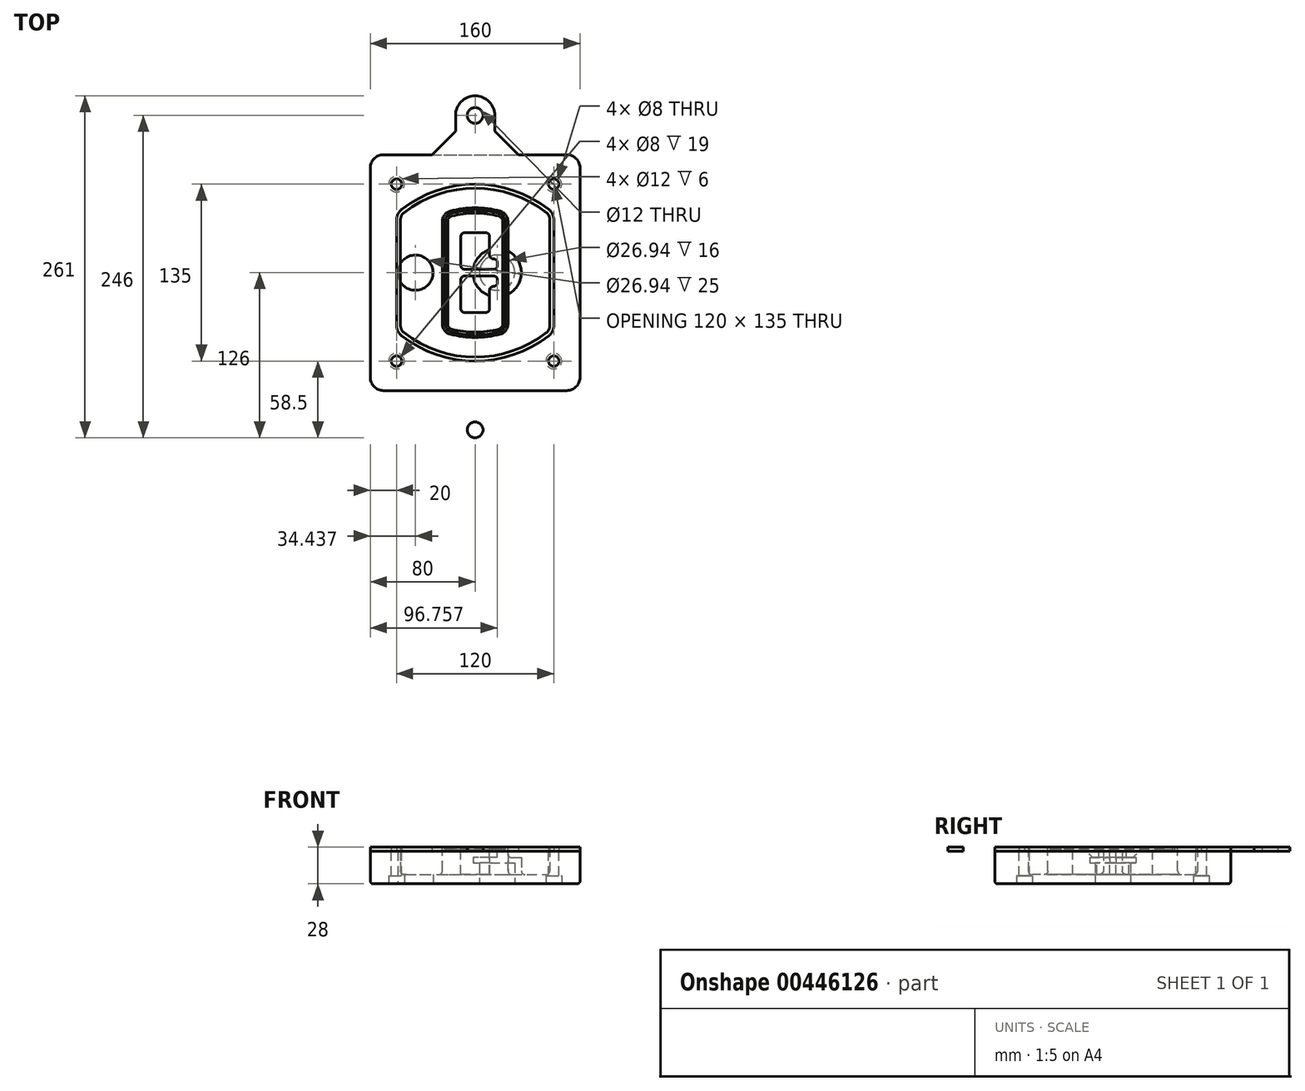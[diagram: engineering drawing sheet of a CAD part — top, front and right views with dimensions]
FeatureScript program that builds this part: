
annotation { "Feature Type Name" : "Feature", "Feature Type Description" : "" }
export const myFeature = defineFeature(function(context is Context, id is Id, definition is map)
    precondition{}
    {
        {
            var Q0;
            Q0=qCreatedBy(makeId("Top.planeOp"),FACE);
            var sketch = newSketch(context, id + "F0", { "sketchPlane" : qUnion([Q0])});
            skPoint(sketch, "E0.rect.middle", {"position": v(0, 0) * mm});
            skLineSegment(sketch, "E1.bottom", {"start": v(-70, -90) * mm, "end": v(70, -90) * mm});
            skLineSegment(sketch, "E1.top", {"start": v(-70, 90) * mm, "end": v(70, 90) * mm});
            skLineSegment(sketch, "E1.left", {"start": v(-80, -80) * mm, "end": v(-80, 80) * mm});
            skLineSegment(sketch, "E1.right", {"start": v(80, -80) * mm, "end": v(80, 80) * mm});
            skLineSegment(sketch, "E2", {"start": v(-80, 90) * mm, "end": v(80, -90) * mm, "construction": true});
            skLineSegment(sketch, "E3", {"start": v(80, 90) * mm, "end": v(-80, -90) * mm, "construction": true});
            skCircle(sketch, "E4", {"center": v(-60, 67.5) * mm, "radius": 4 * mm});
            skCircle(sketch, "E5", {"center": v(60, 67.5) * mm, "radius": 4 * mm});
            skCircle(sketch, "E6", {"center": v(60, -67.5) * mm, "radius": 4 * mm});
            skCircle(sketch, "E7", {"center": v(-60, -67.5) * mm, "radius": 4 * mm});
            skLineSegment(sketch, "E8", {"start": v(-60, 67.5) * mm, "end": v(60, 67.5) * mm, "construction": true});
            skLineSegment(sketch, "E9", {"start": v(60, 67.5) * mm, "end": v(60, -67.5) * mm, "construction": true});
            skLineSegment(sketch, "E10", {"start": v(60, -67.5) * mm, "end": v(-60, -67.5) * mm, "construction": true});
            skLineSegment(sketch, "E11", {"start": v(-60, -67.5) * mm, "end": v(-60, 67.5) * mm, "construction": true});
            skLineSegment(sketch, "E12", {"start": v(-60, 40.3) * mm, "end": v(-60, -40.3) * mm});
            skLineSegment(sketch, "E13", {"start": v(60, 40.3) * mm, "end": v(60, -40.3) * mm});
            skArc(sketch, "E14", {"start": v(56.15, 48.18) * mm, "mid": v(0, 67.5) * mm, "end": v(-56.15, 48.18) * mm});
            skArc(sketch, "E15", {"start": v(-56.15, -48.18) * mm, "mid": v(0, -67.5) * mm, "end": v(56.15, -48.18) * mm});
            skLineSegment(sketch, "E16", {"start": v(-60, 0) * mm, "end": v(60, 0) * mm, "construction": true});
            skPoint(sketch, "E17.visualSharp", {"position": v(-60, -45) * mm});
            skArc(sketch, "E17.filletArc", {"start": v(-60, -40.3) * mm, "mid": v(-58.99, -44.68) * mm, "end": v(-56.15, -48.18) * mm});
            skPoint(sketch, "E18.visualSharp", {"position": v(-60, 45) * mm});
            skArc(sketch, "E18.filletArc", {"start": v(-56.15, 48.18) * mm, "mid": v(-58.99, 44.68) * mm, "end": v(-60, 40.3) * mm});
            skPoint(sketch, "E19.visualSharp", {"position": v(60, 45) * mm});
            skArc(sketch, "E19.filletArc", {"start": v(60, 40.3) * mm, "mid": v(58.99, 44.68) * mm, "end": v(56.15, 48.18) * mm});
            skPoint(sketch, "E20.visualSharp", {"position": v(60, -45) * mm});
            skArc(sketch, "E20.filletArc", {"start": v(56.15, -48.18) * mm, "mid": v(58.99, -44.68) * mm, "end": v(60, -40.3) * mm});
            skPoint(sketch, "E21.visualSharp", {"position": v(-80, 90) * mm});
            skArc(sketch, "E21.filletArc", {"start": v(-70, 90) * mm, "mid": v(-77.07, 87.07) * mm, "end": v(-80, 80) * mm});
            skPoint(sketch, "E22.visualSharp", {"position": v(80, 90) * mm});
            skArc(sketch, "E22.filletArc", {"start": v(80, 80) * mm, "mid": v(77.07, 87.07) * mm, "end": v(70, 90) * mm});
            skPoint(sketch, "E23.visualSharp", {"position": v(80, -90) * mm});
            skArc(sketch, "E23.filletArc", {"start": v(70, -90) * mm, "mid": v(77.07, -87.07) * mm, "end": v(80, -80) * mm});
            skPoint(sketch, "E24.visualSharp", {"position": v(-80, -90) * mm});
            skArc(sketch, "E24.filletArc", {"start": v(-80, -80) * mm, "mid": v(-77.07, -87.07) * mm, "end": v(-70, -90) * mm});
            skArc(sketch, "E25.0", {"start": v(57, 40.3) * mm, "mid": v(56.3, 43.36) * mm, "end": v(54.3, 45.81) * mm});
            skLineSegment(sketch, "E25.1", {"start": v(57, 40.3) * mm, "end": v(57, -40.3) * mm});
            skArc(sketch, "E25.2", {"start": v(54.3, -45.81) * mm, "mid": v(56.3, -43.36) * mm, "end": v(57, -40.3) * mm});
            skArc(sketch, "E25.3", {"start": v(-54.3, -45.81) * mm, "mid": v(0, -64.5) * mm, "end": v(54.3, -45.81) * mm});
            skArc(sketch, "E25.4", {"start": v(-57, -40.3) * mm, "mid": v(-56.3, -43.36) * mm, "end": v(-54.3, -45.81) * mm});
            skArc(sketch, "E25.5", {"start": v(54.3, 45.81) * mm, "mid": v(0, 64.5) * mm, "end": v(-54.3, 45.81) * mm});
            skLineSegment(sketch, "E25.6", {"start": v(-57, 40.3) * mm, "end": v(-57, -40.3) * mm});
            skArc(sketch, "E25.7", {"start": v(-54.3, 45.81) * mm, "mid": v(-56.3, 43.36) * mm, "end": v(-57, 40.3) * mm});
            skArc(sketch, "E26.0", {"start": v(-58.62, 51.33) * mm, "mid": v(-62.58, 46.43) * mm, "end": v(-64, 40.3) * mm});
            skArc(sketch, "E26.1", {"start": v(58.62, 51.33) * mm, "mid": v(0, 71.5) * mm, "end": v(-58.62, 51.33) * mm});
            skArc(sketch, "E26.2", {"start": v(64, 40.3) * mm, "mid": v(62.58, 46.43) * mm, "end": v(58.62, 51.33) * mm});
            skLineSegment(sketch, "E26.3", {"start": v(64, 40.3) * mm, "end": v(64, -40.3) * mm});
            skArc(sketch, "E26.4", {"start": v(58.62, -51.33) * mm, "mid": v(62.58, -46.43) * mm, "end": v(64, -40.3) * mm});
            skLineSegment(sketch, "E26.5", {"start": v(-64, 40.3) * mm, "end": v(-64, -40.3) * mm});
            skArc(sketch, "E26.6", {"start": v(-58.62, -51.33) * mm, "mid": v(0, -71.5) * mm, "end": v(58.62, -51.33) * mm});
            skArc(sketch, "E26.7", {"start": v(-64, -40.3) * mm, "mid": v(-62.58, -46.43) * mm, "end": v(-58.62, -51.33) * mm});
            skSolve(sketch);
        }
        {
            var Q0;
            Q0=makeQuery(id+"F0.imprint","IMPRINT",FACE,{"disambiguationData":[TD([[makeQuery(id+"F0.imprint","IMPRINT",EDGE,{"derivedFrom":sQuery(id+"F0.wireOp",EDGE,"E1.bottom")}),1.0]])]});
            var Q1;
            Q1=makeQuery(id+"F0.imprint","IMPRINT",FACE,{"disambiguationData":[TD([[makeQuery(id+"F0.imprint","IMPRINT",EDGE,{"derivedFrom":sQuery(id+"F0.wireOp",EDGE,"E12")}),1.0]])]});
            var Q2;
            Q2=makeQuery(id+"F0.imprint","IMPRINT",FACE,{"disambiguationData":[TD([[makeQuery(id+"F0.imprint","IMPRINT",EDGE,{"derivedFrom":sQuery(id+"F0.wireOp",EDGE,"E25.0")}),1.0]])]});
            var Q3;
            Q3=makeQuery(id+"F0.imprint","IMPRINT",FACE,{"disambiguationData":[TD([[makeQuery(id+"F0.imprint","IMPRINT",EDGE,{"derivedFrom":sQuery(id+"F0.wireOp",EDGE,"E12")}),-1.0]])]});
            extrude(context, id + "F1", {"entities" : qUnion([Q0, Q1, Q2, Q3]), "oppositeDirection" : true, "depth" : 25 * mm});
        }
        {
            var Q0;
            Q0=makeQuery(id+"F0.imprint","IMPRINT",FACE,{"disambiguationData":[TD([[makeQuery(id+"F0.imprint","IMPRINT",EDGE,{"derivedFrom":sQuery(id+"F0.wireOp",EDGE,"E12")}),1.0]])]});
            extrude(context, id + "F2", {"entities" : qUnion([Q0]), "operationType" : NewBodyOperationType.ADD, "depth" : 3 * mm});
        }
        {
            var Q0;
            Q0=makeQuery(id+"F0.imprint","IMPRINT",FACE,{"disambiguationData":[TD([[makeQuery(id+"F0.imprint","IMPRINT",EDGE,{"derivedFrom":sQuery(id+"F0.wireOp",EDGE,"E25.0")}),1.0]])]});
            extrude(context, id + "F3", {"entities" : qUnion([Q0]), "operationType" : NewBodyOperationType.REMOVE, "oppositeDirection" : true, "depth" : 18 * mm});
        }
        {
            var Q0;
            Q0=makeQuery(id+"F2.opExtrude","CAP_FACE",FACE,{"disambiguationData":[OSD([sQuery(id+"F0.wireOp",EDGE,"E12"),sQuery(id+"F0.wireOp",EDGE,"E13"),sQuery(id+"F0.wireOp",EDGE,"E14"),sQuery(id+"F0.wireOp",EDGE,"E15"),sQuery(id+"F0.wireOp",EDGE,"E17.filletArc"),sQuery(id+"F0.wireOp",EDGE,"E18.filletArc"),sQuery(id+"F0.wireOp",EDGE,"E19.filletArc"),sQuery(id+"F0.wireOp",EDGE,"E20.filletArc"),sQuery(id+"F0.wireOp",EDGE,"E25.0"),sQuery(id+"F0.wireOp",EDGE,"E25.1"),sQuery(id+"F0.wireOp",EDGE,"E25.2"),sQuery(id+"F0.wireOp",EDGE,"E25.3"),sQuery(id+"F0.wireOp",EDGE,"E25.4"),sQuery(id+"F0.wireOp",EDGE,"E25.5"),sQuery(id+"F0.wireOp",EDGE,"E25.6"),sQuery(id+"F0.wireOp",EDGE,"E25.7")])],"isStart":false});
            var sketch = newSketch(context, id + "F4", { "sketchPlane" : qUnion([Q0])});
            skArc(sketch, "E27.0", {"start": v(-19.08, -46.97) * mm, "mid": v(0, -49.5) * mm, "end": v(19.08, -46.97) * mm});
            skArc(sketch, "E28.0", {"start": v(19.08, 46.97) * mm, "mid": v(0, 49.5) * mm, "end": v(-19.08, 46.97) * mm});
            skLineSegment(sketch, "E29", {"start": v(-25, 39.25) * mm, "end": v(-25, -39.25) * mm});
            skLineSegment(sketch, "E30", {"start": v(25, 39.25) * mm, "end": v(25, -39.25) * mm});
            skLineSegment(sketch, "E31", {"start": v(-25, 45.1) * mm, "end": v(25, 45.1) * mm, "construction": true});
            skLineSegment(sketch, "E32", {"start": v(-25, -45.1) * mm, "end": v(25, -45.1) * mm, "construction": true});
            skPoint(sketch, "E33.visualSharp", {"position": v(-25, 45.1) * mm});
            skArc(sketch, "E33.filletArc", {"start": v(-19.08, 46.97) * mm, "mid": v(-23.35, 44.11) * mm, "end": v(-25, 39.25) * mm});
            skPoint(sketch, "E34.visualSharp", {"position": v(25, 45.1) * mm});
            skArc(sketch, "E34.filletArc", {"start": v(25, 39.25) * mm, "mid": v(23.35, 44.11) * mm, "end": v(19.08, 46.97) * mm});
            skPoint(sketch, "E35.visualSharp", {"position": v(25, -45.1) * mm});
            skArc(sketch, "E35.filletArc", {"start": v(19.08, -46.97) * mm, "mid": v(23.35, -44.11) * mm, "end": v(25, -39.25) * mm});
            skPoint(sketch, "E36.visualSharp", {"position": v(-25, -45.1) * mm});
            skArc(sketch, "E36.filletArc", {"start": v(-25, -39.25) * mm, "mid": v(-23.35, -44.11) * mm, "end": v(-19.08, -46.97) * mm});
            skArc(sketch, "E37.0", {"start": v(54.3, 45.81) * mm, "mid": v(0, 64.5) * mm, "end": v(-54.3, 45.81) * mm});
            skArc(sketch, "E37.1", {"start": v(-54.3, 45.81) * mm, "mid": v(-56.3, 43.36) * mm, "end": v(-57, 40.3) * mm});
            skLineSegment(sketch, "E37.2", {"start": v(-57, 40.3) * mm, "end": v(-57, -40.3) * mm});
            skArc(sketch, "E37.3", {"start": v(-57, -40.3) * mm, "mid": v(-56.3, -43.36) * mm, "end": v(-54.3, -45.81) * mm});
            skArc(sketch, "E37.4", {"start": v(-54.3, -45.81) * mm, "mid": v(0, -64.5) * mm, "end": v(54.3, -45.81) * mm});
            skArc(sketch, "E37.5", {"start": v(54.3, -45.81) * mm, "mid": v(56.3, -43.36) * mm, "end": v(57, -40.3) * mm});
            skLineSegment(sketch, "E37.6", {"start": v(57, 40.3) * mm, "end": v(57, -40.3) * mm});
            skArc(sketch, "E37.7", {"start": v(57, 40.3) * mm, "mid": v(56.3, 43.36) * mm, "end": v(54.3, 45.81) * mm});
            skLineSegment(sketch, "E38.0", {"start": v(23, 39.25) * mm, "end": v(23, -39.25) * mm});
            skArc(sketch, "E38.1", {"start": v(18.56, -45.04) * mm, "mid": v(21.76, -42.9) * mm, "end": v(23, -39.25) * mm});
            skArc(sketch, "E38.2", {"start": v(-18.56, -45.04) * mm, "mid": v(0, -47.5) * mm, "end": v(18.56, -45.04) * mm});
            skArc(sketch, "E38.3", {"start": v(-23, -39.25) * mm, "mid": v(-21.76, -42.9) * mm, "end": v(-18.56, -45.04) * mm});
            skLineSegment(sketch, "E38.4", {"start": v(-23, 39.25) * mm, "end": v(-23, -39.25) * mm});
            skArc(sketch, "E38.5", {"start": v(23, 39.25) * mm, "mid": v(21.76, 42.9) * mm, "end": v(18.56, 45.04) * mm});
            skArc(sketch, "E38.6", {"start": v(-18.56, 45.04) * mm, "mid": v(-21.76, 42.9) * mm, "end": v(-23, 39.25) * mm});
            skArc(sketch, "E38.7", {"start": v(18.56, 45.04) * mm, "mid": v(0, 47.5) * mm, "end": v(-18.56, 45.04) * mm});
            skArc(sketch, "E39.0", {"start": v(21, 39.25) * mm, "mid": v(20.18, 41.68) * mm, "end": v(18.04, 43.1) * mm});
            skLineSegment(sketch, "E39.1", {"start": v(21, 39.25) * mm, "end": v(21, -39.25) * mm});
            skArc(sketch, "E39.2", {"start": v(18.04, -43.1) * mm, "mid": v(20.18, -41.68) * mm, "end": v(21, -39.25) * mm});
            skArc(sketch, "E39.3", {"start": v(-18.04, -43.1) * mm, "mid": v(0, -45.5) * mm, "end": v(18.04, -43.1) * mm});
            skArc(sketch, "E39.4", {"start": v(-21, -39.25) * mm, "mid": v(-20.18, -41.68) * mm, "end": v(-18.04, -43.1) * mm});
            skArc(sketch, "E39.5", {"start": v(18.04, 43.1) * mm, "mid": v(0, 45.5) * mm, "end": v(-18.04, 43.1) * mm});
            skLineSegment(sketch, "E39.6", {"start": v(-21, 39.25) * mm, "end": v(-21, -39.25) * mm});
            skArc(sketch, "E39.7", {"start": v(-18.04, 43.1) * mm, "mid": v(-20.18, 41.68) * mm, "end": v(-21, 39.25) * mm});
            skLineSegment(sketch, "E40", {"start": v(-25, 0) * mm, "end": v(25, 0) * mm, "construction": true});
            skLineSegment(sketch, "E41", {"start": v(-11, 5.5) * mm, "end": v(-11, 27.5) * mm});
            skLineSegment(sketch, "E42", {"start": v(-8, 30.5) * mm, "end": v(8, 30.5) * mm});
            skLineSegment(sketch, "E43", {"start": v(11, 27.5) * mm, "end": v(11, 13.5) * mm});
            skLineSegment(sketch, "E44", {"start": v(14, 10.5) * mm, "end": v(14, 10.5) * mm});
            skLineSegment(sketch, "E45", {"start": v(17, 7.5) * mm, "end": v(17, 5.5) * mm});
            skLineSegment(sketch, "E46", {"start": v(14, 2.5) * mm, "end": v(-8, 2.5) * mm});
            skPoint(sketch, "E47.visualSharp", {"position": v(-11, 30.5) * mm});
            skArc(sketch, "E47.filletArc", {"start": v(-8, 30.5) * mm, "mid": v(-10.12, 29.62) * mm, "end": v(-11, 27.5) * mm});
            skPoint(sketch, "E48.visualSharp", {"position": v(11, 30.5) * mm});
            skArc(sketch, "E48.filletArc", {"start": v(11, 27.5) * mm, "mid": v(10.12, 29.62) * mm, "end": v(8, 30.5) * mm});
            skPoint(sketch, "E49.visualSharp", {"position": v(11, 10.5) * mm});
            skArc(sketch, "E49.filletArc", {"start": v(11, 13.5) * mm, "mid": v(11.88, 11.38) * mm, "end": v(14, 10.5) * mm});
            skPoint(sketch, "E50.visualSharp", {"position": v(17, 10.5) * mm});
            skArc(sketch, "E50.filletArc", {"start": v(17, 7.5) * mm, "mid": v(16.12, 9.62) * mm, "end": v(14, 10.5) * mm});
            skPoint(sketch, "E51.visualSharp", {"position": v(17, 2.5) * mm});
            skArc(sketch, "E51.filletArc", {"start": v(14, 2.5) * mm, "mid": v(16.12, 3.38) * mm, "end": v(17, 5.5) * mm});
            skPoint(sketch, "E52.visualSharp", {"position": v(-11, 2.5) * mm});
            skArc(sketch, "E52.filletArc", {"start": v(-11, 5.5) * mm, "mid": v(-10.12, 3.38) * mm, "end": v(-8, 2.5) * mm});
            skLineSegment(sketch, "E53.0.MirrorCS", {"start": v(14, -2.5) * mm, "end": v(-8, -2.5) * mm});
            skArc(sketch, "E54.0.MirrorCS", {"start": v(-11, -5.5) * mm, "mid": v(-10.12, -3.38) * mm, "end": v(-8, -2.5) * mm});
            skLineSegment(sketch, "E55.0.MirrorCS", {"start": v(-11, -5.5) * mm, "end": v(-11, -27.5) * mm});
            skArc(sketch, "E56.0.MirrorCS", {"start": v(-8, -30.5) * mm, "mid": v(-10.12, -29.62) * mm, "end": v(-11, -27.5) * mm});
            skLineSegment(sketch, "E57.0.MirrorCS", {"start": v(-8, -30.5) * mm, "end": v(8, -30.5) * mm});
            skArc(sketch, "E58.0.MirrorCS", {"start": v(11, -27.5) * mm, "mid": v(10.12, -29.62) * mm, "end": v(8, -30.5) * mm});
            skLineSegment(sketch, "E59.0.MirrorCS", {"start": v(11, -27.5) * mm, "end": v(11, -13.5) * mm});
            skArc(sketch, "E60.0.MirrorCS", {"start": v(11, -13.5) * mm, "mid": v(11.88, -11.38) * mm, "end": v(14, -10.5) * mm});
            skArc(sketch, "E61.0.MirrorCS", {"start": v(17, -7.5) * mm, "mid": v(16.12, -9.62) * mm, "end": v(14, -10.5) * mm});
            skLineSegment(sketch, "E62.0.MirrorCS", {"start": v(17, -7.5) * mm, "end": v(17, -5.5) * mm});
            skArc(sketch, "E63.0.MirrorCS", {"start": v(14, -2.5) * mm, "mid": v(16.12, -3.38) * mm, "end": v(17, -5.5) * mm});
            skSolve(sketch);
        }
        {
            var Q0;
            Q0=makeQuery(id+"F4.imprint","IMPRINT",FACE,{"disambiguationData":[TD([[makeQuery(id+"F4.imprint","IMPRINT",EDGE,{"derivedFrom":sQuery(id+"F4.wireOp",EDGE,"E27.0")}),1.0]])]});
            var Q1;
            Q1=makeQuery(id+"F4.imprint","IMPRINT",FACE,{"disambiguationData":[TD([[makeQuery(id+"F4.imprint","IMPRINT",EDGE,{"derivedFrom":sQuery(id+"F4.wireOp",EDGE,"E38.0")}),-1.0]])]});
            var Q2;
            Q2=makeQuery(id+"F4.imprint","IMPRINT",FACE,{"disambiguationData":[TD([[makeQuery(id+"F4.imprint","IMPRINT",EDGE,{"derivedFrom":sQuery(id+"F4.wireOp",EDGE,"E39.0")}),1.0]])]});
            extrude(context, id + "F5", {"entities" : qUnion([Q0, Q1, Q2]), "operationType" : NewBodyOperationType.ADD, "endBound" : BoundingType.UP_TO_NEXT, "oppositeDirection" : true, "depth" : 25 * mm});
        }
        {
            var Q0;
            Q0=makeQuery(id+"F4.imprint","IMPRINT",FACE,{"disambiguationData":[TD([[makeQuery(id+"F4.imprint","IMPRINT",EDGE,{"derivedFrom":sQuery(id+"F4.wireOp",EDGE,"E38.0")}),-1.0]])]});
            extrude(context, id + "F6", {"entities" : qUnion([Q0]), "operationType" : NewBodyOperationType.REMOVE, "oppositeDirection" : true, "depth" : 2 * mm});
        }
        {
            var Q0;
            Q0=makeQuery(id+"F1.opExtrude","CAP_FACE",FACE,{"disambiguationData":[OSD([sQuery(id+"F0.wireOp",EDGE,"E1.bottom"),sQuery(id+"F0.wireOp",EDGE,"E1.top"),sQuery(id+"F0.wireOp",EDGE,"E1.left"),sQuery(id+"F0.wireOp",EDGE,"E1.right"),sQuery(id+"F0.wireOp",EDGE,"E4"),sQuery(id+"F0.wireOp",EDGE,"E5"),sQuery(id+"F0.wireOp",EDGE,"E6"),sQuery(id+"F0.wireOp",EDGE,"E7"),sQuery(id+"F0.wireOp",EDGE,"E21.filletArc"),sQuery(id+"F0.wireOp",EDGE,"E22.filletArc"),sQuery(id+"F0.wireOp",EDGE,"E23.filletArc"),sQuery(id+"F0.wireOp",EDGE,"E24.filletArc")])],"isStart":false});
            var sketch = newSketch(context, id + "F7", { "sketchPlane" : qUnion([Q0])});
            skCircle(sketch, "E64", {"center": v(16.76, 0) * mm, "radius": 13.47 * mm});
            skCircle(sketch, "E65", {"center": v(-45.56, 0) * mm, "radius": 13.47 * mm});
            skLineSegment(sketch, "E66", {"start": v(80, 0) * mm, "end": v(-80, 0) * mm});
            skCircle(sketch, "E67", {"center": v(16.76, 0) * mm, "radius": 18.47 * mm});
            skCircle(sketch, "E68", {"center": v(60, -67.5) * mm, "radius": 6 * mm});
            skCircle(sketch, "E69", {"center": v(-60, -67.5) * mm, "radius": 6 * mm});
            skCircle(sketch, "E70", {"center": v(-60, 67.5) * mm, "radius": 6 * mm});
            skCircle(sketch, "E71", {"center": v(60, 67.5) * mm, "radius": 6 * mm});
            skSolve(sketch);
        }
        {
            var Q0;
            {var subQ1=sQuery(id+"F7.wireOp",EDGE,"E66");var subQ4=sQuery(id+"F7.wireOp",EDGE,"E64");var subQ6=makeQuery(id+"F7.imprint","INTERSECT",VERTEX,{"disambiguationData":[OD(0.0)],"derivedFrom":[subQ4,subQ1]});Q0=makeQuery(id+"F7.imprint","IMPRINT",FACE,{"disambiguationData":[TD([[makeQuery(id+"F7.imprint","IMPRINT",EDGE,{"disambiguationData":[TD([[subQ6,-1.0]])],"derivedFrom":subQ4}),-1.0]])]});}
            var Q1;
            {var subQ0=sQuery(id+"F7.wireOp",EDGE,"E66");var subQ1=sQuery(id+"F7.wireOp",EDGE,"E64");var subQ3=makeQuery(id+"F7.imprint","INTERSECT",VERTEX,{"disambiguationData":[OD(0.0)],"derivedFrom":[subQ1,subQ0]});Q1=makeQuery(id+"F7.imprint","IMPRINT",FACE,{"disambiguationData":[TD([[makeQuery(id+"F7.imprint","IMPRINT",EDGE,{"disambiguationData":[TD([[subQ3,-1.0]])],"derivedFrom":subQ1}),1.0]])]});}
            var Q2;
            {var subQ0=sQuery(id+"F7.wireOp",EDGE,"E66");var subQ1=sQuery(id+"F7.wireOp",EDGE,"E64");var subQ3=makeQuery(id+"F7.imprint","INTERSECT",VERTEX,{"disambiguationData":[OD(0.0)],"derivedFrom":[subQ1,subQ0]});Q2=makeQuery(id+"F7.imprint","IMPRINT",FACE,{"disambiguationData":[TD([[makeQuery(id+"F7.imprint","IMPRINT",EDGE,{"disambiguationData":[TD([[subQ3,1.0]])],"derivedFrom":subQ1}),1.0]])]});}
            var Q3;
            {var subQ1=sQuery(id+"F7.wireOp",EDGE,"E66");var subQ4=sQuery(id+"F7.wireOp",EDGE,"E64");var subQ6=makeQuery(id+"F7.imprint","INTERSECT",VERTEX,{"disambiguationData":[OD(0.0)],"derivedFrom":[subQ4,subQ1]});Q3=makeQuery(id+"F7.imprint","IMPRINT",FACE,{"disambiguationData":[TD([[makeQuery(id+"F7.imprint","IMPRINT",EDGE,{"disambiguationData":[TD([[subQ6,1.0]])],"derivedFrom":subQ4}),-1.0]])]});}
            extrude(context, id + "F8", {"entities" : qUnion([Q0, Q1, Q2, Q3]), "operationType" : NewBodyOperationType.ADD, "oppositeDirection" : true, "depth" : 20 * mm});
        }
        {
            var Q0;
            {var subQ0=sQuery(id+"F7.wireOp",EDGE,"E66");var subQ1=sQuery(id+"F7.wireOp",EDGE,"E64");var subQ3=makeQuery(id+"F7.imprint","INTERSECT",VERTEX,{"disambiguationData":[OD(0.0)],"derivedFrom":[subQ1,subQ0]});Q0=makeQuery(id+"F7.imprint","IMPRINT",FACE,{"disambiguationData":[TD([[makeQuery(id+"F7.imprint","IMPRINT",EDGE,{"disambiguationData":[TD([[subQ3,-1.0]])],"derivedFrom":subQ1}),1.0]])]});}
            var Q1;
            {var subQ0=sQuery(id+"F7.wireOp",EDGE,"E66");var subQ1=sQuery(id+"F7.wireOp",EDGE,"E64");var subQ3=makeQuery(id+"F7.imprint","INTERSECT",VERTEX,{"disambiguationData":[OD(0.0)],"derivedFrom":[subQ1,subQ0]});Q1=makeQuery(id+"F7.imprint","IMPRINT",FACE,{"disambiguationData":[TD([[makeQuery(id+"F7.imprint","IMPRINT",EDGE,{"disambiguationData":[TD([[subQ3,1.0]])],"derivedFrom":subQ1}),1.0]])]});}
            extrude(context, id + "F9", {"entities" : qUnion([Q0, Q1]), "operationType" : NewBodyOperationType.REMOVE, "oppositeDirection" : true, "depth" : 16 * mm});
        }
        {
            var Q0;
            {var subQ0=sQuery(id+"F7.wireOp",EDGE,"E66");var subQ1=sQuery(id+"F7.wireOp",EDGE,"E65");var subQ3=makeQuery(id+"F7.imprint","INTERSECT",VERTEX,{"disambiguationData":[OD(0.0)],"derivedFrom":[subQ1,subQ0]});Q0=makeQuery(id+"F7.imprint","IMPRINT",FACE,{"disambiguationData":[TD([[makeQuery(id+"F7.imprint","IMPRINT",EDGE,{"disambiguationData":[TD([[subQ3,-1.0]])],"derivedFrom":subQ1}),1.0]])]});}
            var Q1;
            {var subQ0=sQuery(id+"F7.wireOp",EDGE,"E66");var subQ1=sQuery(id+"F7.wireOp",EDGE,"E65");var subQ3=makeQuery(id+"F7.imprint","INTERSECT",VERTEX,{"disambiguationData":[OD(0.0)],"derivedFrom":[subQ1,subQ0]});Q1=makeQuery(id+"F7.imprint","IMPRINT",FACE,{"disambiguationData":[TD([[makeQuery(id+"F7.imprint","IMPRINT",EDGE,{"disambiguationData":[TD([[subQ3,1.0]])],"derivedFrom":subQ1}),1.0]])]});}
            extrude(context, id + "F10", {"entities" : qUnion([Q0, Q1]), "operationType" : NewBodyOperationType.REMOVE, "oppositeDirection" : true, "depth" : 25 * mm});
        }
        {
            var Q0;
            Q0=makeQuery(id+"F7.imprint","IMPRINT",FACE,{"disambiguationData":[TD([[makeQuery(id+"F7.imprint","IMPRINT",EDGE,{"derivedFrom":sQuery(id+"F7.wireOp",EDGE,"E68")}),1.0]])]});
            var Q1;
            Q1=makeQuery(id+"F7.imprint","IMPRINT",FACE,{"disambiguationData":[TD([[makeQuery(id+"F7.imprint","IMPRINT",EDGE,{"derivedFrom":makeQuery(id+"F1.opExtrude","CAP_EDGE",EDGE,{"disambiguationData":[OSD([sQuery(id+"F0.wireOp",EDGE,"E5")])],"isStart":false})}),-1.0]])]});
            var Q2;
            Q2=makeQuery(id+"F7.imprint","IMPRINT",FACE,{"disambiguationData":[TD([[makeQuery(id+"F7.imprint","IMPRINT",EDGE,{"derivedFrom":sQuery(id+"F7.wireOp",EDGE,"E69")}),1.0]])]});
            var Q3;
            Q3=makeQuery(id+"F7.imprint","IMPRINT",FACE,{"disambiguationData":[TD([[makeQuery(id+"F7.imprint","IMPRINT",EDGE,{"derivedFrom":makeQuery(id+"F1.opExtrude","CAP_EDGE",EDGE,{"disambiguationData":[OSD([sQuery(id+"F0.wireOp",EDGE,"E4")])],"isStart":false})}),-1.0]])]});
            var Q4;
            Q4=makeQuery(id+"F7.imprint","IMPRINT",FACE,{"disambiguationData":[TD([[makeQuery(id+"F7.imprint","IMPRINT",EDGE,{"derivedFrom":sQuery(id+"F7.wireOp",EDGE,"E70")}),1.0]])]});
            var Q5;
            Q5=makeQuery(id+"F7.imprint","IMPRINT",FACE,{"disambiguationData":[TD([[makeQuery(id+"F7.imprint","IMPRINT",EDGE,{"derivedFrom":makeQuery(id+"F1.opExtrude","CAP_EDGE",EDGE,{"disambiguationData":[OSD([sQuery(id+"F0.wireOp",EDGE,"E7")])],"isStart":false})}),-1.0]])]});
            var Q6;
            Q6=makeQuery(id+"F7.imprint","IMPRINT",FACE,{"disambiguationData":[TD([[makeQuery(id+"F7.imprint","IMPRINT",EDGE,{"derivedFrom":sQuery(id+"F7.wireOp",EDGE,"E71")}),1.0]])]});
            var Q7;
            Q7=makeQuery(id+"F7.imprint","IMPRINT",FACE,{"disambiguationData":[TD([[makeQuery(id+"F7.imprint","IMPRINT",EDGE,{"derivedFrom":makeQuery(id+"F1.opExtrude","CAP_EDGE",EDGE,{"disambiguationData":[OSD([sQuery(id+"F0.wireOp",EDGE,"E6")])],"isStart":false})}),-1.0]])]});
            extrude(context, id + "F11", {"entities" : qUnion([Q0, Q1, Q2, Q3, Q4, Q5, Q6, Q7]), "operationType" : NewBodyOperationType.REMOVE, "oppositeDirection" : true, "depth" : 6 * mm});
        }
        {
            var Q0;
            Q0=makeQuery(id+"F9.boolean.opBoolean","COPY",FACE,{"derivedFrom":makeQuery(id+"F9.opExtrude","CAP_FACE",FACE,{"disambiguationData":[OSD([sQuery(id+"F7.wireOp",EDGE,"E64")])],"isStart":false})});
            var sketch = newSketch(context, id + "F12", { "sketchPlane" : qUnion([Q0])});
            skArc(sketch, "E72.0", {"start": v(11, 17.55) * mm, "mid": v(2.57, 11.82) * mm, "end": v(-1.54, 2.5) * mm});
            skArc(sketch, "E72.1", {"start": v(-1.54, -2.5) * mm, "mid": v(2.57, -11.82) * mm, "end": v(11, -17.55) * mm});
            skLineSegment(sketch, "E73", {"start": v(-1.54, -2.5) * mm, "end": v(14, -2.5) * mm});
            skLineSegment(sketch, "E74.0", {"start": v(14, 2.5) * mm, "end": v(-1.54, 2.5) * mm});
            skArc(sketch, "E74.1", {"start": v(14, 2.5) * mm, "mid": v(16.12, 3.38) * mm, "end": v(17, 5.5) * mm});
            skLineSegment(sketch, "E74.2", {"start": v(17, 7.5) * mm, "end": v(17, 5.5) * mm});
            skArc(sketch, "E74.3", {"start": v(17, 7.5) * mm, "mid": v(16.12, 9.62) * mm, "end": v(14, 10.5) * mm});
            skArc(sketch, "E74.4", {"start": v(11, 13.5) * mm, "mid": v(11.88, 11.38) * mm, "end": v(14, 10.5) * mm});
            skLineSegment(sketch, "E74.5", {"start": v(11, 17.55) * mm, "end": v(11, 13.5) * mm});
            skLineSegment(sketch, "E74.7", {"start": v(14, -2.5) * mm, "end": v(-1.54, -2.5) * mm});
            skArc(sketch, "E74.8", {"start": v(14, -2.5) * mm, "mid": v(16.12, -3.38) * mm, "end": v(17, -5.5) * mm});
            skLineSegment(sketch, "E74.9", {"start": v(17, -7.5) * mm, "end": v(17, -5.5) * mm});
            skArc(sketch, "E74.10", {"start": v(17, -7.5) * mm, "mid": v(16.12, -9.62) * mm, "end": v(14, -10.5) * mm});
            skArc(sketch, "E74.11", {"start": v(11, -13.5) * mm, "mid": v(11.88, -11.38) * mm, "end": v(14, -10.5) * mm});
            skLineSegment(sketch, "E74.12", {"start": v(11, -17.55) * mm, "end": v(11, -13.5) * mm});
            skPoint(sketch, "E75.orphan", {"position": v(11, -27.5) * mm});
            skPoint(sketch, "E76.orphan", {"position": v(-8, -2.5) * mm});
            skPoint(sketch, "E77.orphan", {"position": v(-8, 2.5) * mm});
            skPoint(sketch, "E78.orphan", {"position": v(11, 27.5) * mm});
            skSolve(sketch);
        }
        {
            var Q0;
            {var subQ7=sQuery(id+"F12.wireOp",EDGE,"E72.0");var subQ14=sQuery(id+"F12.wireOp",EDGE,"E72.1");var subQ16=sQuery(id+"F12.wireOp",EDGE,"E74.1");var subQ18=sQuery(id+"F12.wireOp",EDGE,"E74.8");Q0=qUnion([makeQuery(id+"F12.imprint","IMPRINT",FACE,{"disambiguationData":[TD([[makeQuery(id+"F12.imprint","IMPRINT",EDGE,{"derivedFrom":subQ7}),1.0]])]}),makeQuery(id+"F12.imprint","IMPRINT",FACE,{"disambiguationData":[TD([[makeQuery(id+"F12.imprint","IMPRINT",EDGE,{"derivedFrom":subQ14}),1.0]])]}),makeQuery(id+"F12.imprint","IMPRINT",FACE,{"disambiguationData":[TD([[makeQuery(id+"F12.imprint","IMPRINT",EDGE,{"derivedFrom":subQ16}),1.0]])]}),makeQuery(id+"F12.imprint","IMPRINT",FACE,{"disambiguationData":[TD([[makeQuery(id+"F12.imprint","IMPRINT",EDGE,{"derivedFrom":subQ18}),-1.0]])]})]);}
            var Q1;
            Q1=makeQuery(id+"F5.boolean.opBoolean","SPLIT",FACE,{"disambiguationData":[TD([makeQuery(id+"F5.opExtrude","SWEPT_FACE",FACE,{"disambiguationData":[OSD([sQuery(id+"F4.wireOp",EDGE,"E41")])]})])],"derivedFrom":makeQuery(id+"F3.boolean.opBoolean","COPY",FACE,{"derivedFrom":makeQuery(id+"F3.opExtrude","CAP_FACE",FACE,{"disambiguationData":[OSD([sQuery(id+"F0.wireOp",EDGE,"E25.0"),sQuery(id+"F0.wireOp",EDGE,"E25.1"),sQuery(id+"F0.wireOp",EDGE,"E25.2"),sQuery(id+"F0.wireOp",EDGE,"E25.3"),sQuery(id+"F0.wireOp",EDGE,"E25.4"),sQuery(id+"F0.wireOp",EDGE,"E25.5"),sQuery(id+"F0.wireOp",EDGE,"E25.6"),sQuery(id+"F0.wireOp",EDGE,"E25.7")])],"isStart":false})})});
            extrude(context, id + "F13", {"entities" : qUnion([Q0]), "operationType" : NewBodyOperationType.REMOVE, "endBound" : BoundingType.UP_TO_SURFACE, "endBoundEntityFace" : qUnion([Q1]), "depth" : 25 * mm});
        }
        {
            var Q0;
            Q0=makeQuery(id+"F3.boolean.opBoolean","COPY",EDGE,{"derivedFrom":makeQuery(id+"F3.opExtrude","CAP_EDGE",EDGE,{"disambiguationData":[OSD([sQuery(id+"F0.wireOp",EDGE,"E25.6")])],"isStart":false})});
            var Q1;
            Q1=makeQuery(id+"F8.boolean.opBoolean","INTERSECT",EDGE,{"derivedFrom":[makeQuery(id+"F5.opExtrude","SWEPT_FACE",FACE,{"disambiguationData":[OSD([sQuery(id+"F4.wireOp",EDGE,"E30")])]}),makeQuery(id+"F8.opExtrude","CAP_FACE",FACE,{"disambiguationData":[OSD([sQuery(id+"F7.wireOp",EDGE,"E67")])],"isStart":false})]});
            var Q2;
            Q2=makeQuery(id+"F8.boolean.opBoolean","INTERSECT",EDGE,{"disambiguationData":[OD(1.0)],"derivedFrom":[makeQuery(id+"F5.opExtrude","SWEPT_FACE",FACE,{"disambiguationData":[OSD([sQuery(id+"F4.wireOp",EDGE,"E30")])]}),makeQuery(id+"F8.opExtrude","SWEPT_FACE",FACE,{"disambiguationData":[OSD([sQuery(id+"F7.wireOp",EDGE,"E67")])]})]});
            var Q3;
            {var subQ0=sQuery(id+"F4.wireOp",EDGE,"E30");Q3=makeQuery(id+"F8.boolean.opBoolean","SPLIT",EDGE,{"disambiguationData":[TD([makeQuery(id+"F5.opExtrude","SWEPT_FACE",FACE,{"disambiguationData":[OSD([sQuery(id+"F4.wireOp",EDGE,"E35.filletArc")])]})])],"derivedFrom":makeQuery(id+"F5.opExtrude","CAP_EDGE",EDGE,{"disambiguationData":[OSD([subQ0])],"isStart":false})});}
            var Q4;
            {var subQ0=sQuery(id+"F0.wireOp",EDGE,"E25.7");var subQ1=sQuery(id+"F0.wireOp",EDGE,"E25.1");var subQ2=sQuery(id+"F0.wireOp",EDGE,"E25.6");var subQ3=sQuery(id+"F0.wireOp",EDGE,"E25.5");var subQ4=sQuery(id+"F0.wireOp",EDGE,"E25.4");var subQ5=sQuery(id+"F0.wireOp",EDGE,"E25.0");var subQ6=sQuery(id+"F0.wireOp",EDGE,"E25.2");var subQ7=sQuery(id+"F0.wireOp",EDGE,"E25.3");Q4=makeQuery(id+"F8.boolean.opBoolean","INTERSECT",EDGE,{"derivedFrom":[makeQuery(id+"F5.boolean.opBoolean","SPLIT",FACE,{"disambiguationData":[TD([makeQuery(id+"F2.opExtrude","SWEPT_FACE",FACE,{"disambiguationData":[OSD([subQ5])]})])],"derivedFrom":makeQuery(id+"F3.boolean.opBoolean","COPY",FACE,{"derivedFrom":makeQuery(id+"F3.opExtrude","CAP_FACE",FACE,{"disambiguationData":[OSD([subQ5,subQ1,subQ6,subQ7,subQ4,subQ3,subQ2,subQ0])],"isStart":false})})}),makeQuery(id+"F8.opExtrude","SWEPT_FACE",FACE,{"disambiguationData":[OSD([sQuery(id+"F7.wireOp",EDGE,"E67")])]})]});}
            var Q5;
            Q5=makeQuery(id+"F8.boolean.opBoolean","INTERSECT",EDGE,{"disambiguationData":[OD(0.0)],"derivedFrom":[makeQuery(id+"F5.opExtrude","SWEPT_FACE",FACE,{"disambiguationData":[OSD([sQuery(id+"F4.wireOp",EDGE,"E30")])]}),makeQuery(id+"F8.opExtrude","SWEPT_FACE",FACE,{"disambiguationData":[OSD([sQuery(id+"F7.wireOp",EDGE,"E67")])]})]});
            fillet(context, id + "F14", {"entities" : qUnion([Q0, Q1, Q2, Q3, Q4, Q5]), "radius" : 3 * mm, "tangentPropagation" : true, "allowEdgeOverflow" : false});
        }
        {
            var Q0;
            Q0=makeQuery(id+"F1.opExtrude","CAP_EDGE",EDGE,{"disambiguationData":[OSD([sQuery(id+"F0.wireOp",EDGE,"E1.bottom")])],"isStart":false});
            fillet(context, id + "F15", {"entities" : qUnion([Q0]), "radius" : 2 * mm, "tangentPropagation" : true, "allowEdgeOverflow" : false});
        }
        {
            var Q0;
            {var subQ0=sQuery(id+"F0.wireOp",EDGE,"E21.filletArc");var subQ1=sQuery(id+"F0.wireOp",EDGE,"E7");var subQ2=sQuery(id+"F0.wireOp",EDGE,"E6");var subQ3=sQuery(id+"F0.wireOp",EDGE,"E5");var subQ4=sQuery(id+"F0.wireOp",EDGE,"E4");var subQ5=sQuery(id+"F0.wireOp",EDGE,"E22.filletArc");var subQ6=sQuery(id+"F0.wireOp",EDGE,"E1.bottom");var subQ7=sQuery(id+"F0.wireOp",EDGE,"E1.right");var subQ8=sQuery(id+"F0.wireOp",EDGE,"E1.top");var subQ9=sQuery(id+"F0.wireOp",EDGE,"E1.left");var subQ10=sQuery(id+"F0.wireOp",EDGE,"E23.filletArc");var subQ11=sQuery(id+"F0.wireOp",EDGE,"E24.filletArc");Q0=makeQuery(id+"F2.boolean.opBoolean","SPLIT",FACE,{"disambiguationData":[TD([makeQuery(id+"F1.opExtrude","SWEPT_FACE",FACE,{"disambiguationData":[OSD([subQ6])]})])],"derivedFrom":makeQuery(id+"F1.opExtrude","CAP_FACE",FACE,{"disambiguationData":[OSD([subQ6,subQ8,subQ9,subQ7,subQ4,subQ3,subQ2,subQ1,subQ0,subQ5,subQ10,subQ11])],"isStart":true})});}
            var sketch = newSketch(context, id + "F16", { "sketchPlane" : qUnion([Q0])});
            skLineSegment(sketch, "E79", {"start": v(0, 90) * mm, "end": v(0, 120) * mm, "construction": true});
            skCircle(sketch, "E80", {"center": v(0, 120) * mm, "radius": 6 * mm});
            skArc(sketch, "E81", {"start": v(15, 120) * mm, "mid": v(0, 135) * mm, "end": v(-15, 120) * mm});
            skLineSegment(sketch, "E82", {"start": v(-33, 90) * mm, "end": v(-15, 108) * mm});
            skLineSegment(sketch, "E83", {"start": v(-15, 108) * mm, "end": v(-15, 120) * mm});
            skLineSegment(sketch, "E84", {"start": v(33, 90) * mm, "end": v(15, 108) * mm});
            skLineSegment(sketch, "E85", {"start": v(15, 108) * mm, "end": v(15, 120) * mm});
            skLineSegment(sketch, "E86", {"start": v(-80, 0) * mm, "end": v(80, 0) * mm, "construction": true});
            skCircle(sketch, "E87.MirrorC", {"center": v(0, -120) * mm, "radius": 6 * mm});
            skArc(sketch, "E88.MirrorCS", {"start": v(15, -120) * mm, "mid": v(0, -135) * mm, "end": v(-15, -120) * mm});
            skLineSegment(sketch, "E89.MirrorCS", {"start": v(15, -108) * mm, "end": v(15, -120) * mm});
            skLineSegment(sketch, "E90.MirrorCS", {"start": v(-15, -108) * mm, "end": v(-15, -120) * mm});
            skLineSegment(sketch, "E91.MirrorCS", {"start": v(33, -90) * mm, "end": v(15, -108) * mm});
            skLineSegment(sketch, "E92.MirrorCS", {"start": v(-33, -90) * mm, "end": v(-15, -108) * mm});
            skSolve(sketch);
        }
        {
            var Q0;
            Q0=makeQuery(id+"F16.imprint","IMPRINT",FACE,{"disambiguationData":[TD([[makeQuery(id+"F16.imprint","IMPRINT",EDGE,{"derivedFrom":sQuery(id+"F16.wireOp",EDGE,"E87.MirrorC")}),1.0]])]});
            var Q1;
            Q1=makeQuery(id+"F16.imprint","IMPRINT",FACE,{"disambiguationData":[TD([[makeQuery(id+"F16.imprint","IMPRINT",EDGE,{"derivedFrom":sQuery(id+"F16.wireOp",EDGE,"E80")}),-1.0]])]});
            var Q2;
            Q2=makeQuery(id+"F16.imprint","IMPRINT",FACE,{"disambiguationData":[TD([[makeQuery(id+"F16.imprint","IMPRINT",EDGE,{"derivedFrom":makeQuery(id+"F1.opExtrude","CAP_EDGE",EDGE,{"disambiguationData":[OSD([sQuery(id+"F0.wireOp",EDGE,"E1.left")])],"isStart":true})}),-1.0]])]});
            var Q3;
            Q3=makeQuery(id+"F2.opExtrude","CAP_FACE",FACE,{"disambiguationData":[OSD([sQuery(id+"F0.wireOp",EDGE,"E12"),sQuery(id+"F0.wireOp",EDGE,"E13"),sQuery(id+"F0.wireOp",EDGE,"E14"),sQuery(id+"F0.wireOp",EDGE,"E15"),sQuery(id+"F0.wireOp",EDGE,"E17.filletArc"),sQuery(id+"F0.wireOp",EDGE,"E18.filletArc"),sQuery(id+"F0.wireOp",EDGE,"E19.filletArc"),sQuery(id+"F0.wireOp",EDGE,"E20.filletArc"),sQuery(id+"F0.wireOp",EDGE,"E25.0"),sQuery(id+"F0.wireOp",EDGE,"E25.1"),sQuery(id+"F0.wireOp",EDGE,"E25.2"),sQuery(id+"F0.wireOp",EDGE,"E25.3"),sQuery(id+"F0.wireOp",EDGE,"E25.4"),sQuery(id+"F0.wireOp",EDGE,"E25.5"),sQuery(id+"F0.wireOp",EDGE,"E25.6"),sQuery(id+"F0.wireOp",EDGE,"E25.7")])],"isStart":false});
            extrude(context, id + "F17", {"entities" : qUnion([Q0, Q1, Q2]), "endBound" : BoundingType.UP_TO_SURFACE, "endBoundEntityFace" : qUnion([Q3]), "depth" : 25 * mm});
        }
    });
